# Revit family: 7. Электрические нагреватели UTR ELN
name_source: partatom
category: Оборудование
revit_build: Autodesk Revit 2016 (Build: 20151209_0715(x64)
units: mm (PartAtom-declared; Revit-internal decimal feet)

## family parameters
Всегда вертикально = Да
На основе рабочей плоскости = Нет
Общий = Нет
При загрузке вырезать с полостями = Нет
Размер круглого соединителя = Использовать диаметр
Тип детали = Нормальный
Точка расчета площади = Нет

## types (25) — shared parameters
h = 60 мм
Единица измерения = шт.
Завод изготовитель = KORF
Ключевая пометка = Вентиляция
Наименование и тех.хар-ка = Электрический нагреватель воздуха
Раздел = ОВ
Синий = Синий
высота ножек = 50 мм

## per-type parameters (varying)
| type | А | А1 | Б | Б1 | Г | Д | Д1 | Масса единицы | Материал | Мощность, кВт | Сила тока J, А | Силовой кабель | Тип, марка, обозначение | высота | размер В | ширина |
| 50-25 ELN/7,5 | 710 мм | 690 мм | 470 мм | 450 мм | 395 мм | 510 мм | 490 мм | 30 | Сталь серая | 8 Вт | 11,3 | ВВГ 4х2,5/1 | UTR 50-25 ELN/7,5 | 500 мм | 635 мм | 250 мм |
| 50-25 ELN/15 | 710 мм | 690 мм | 470 мм | 450 мм | 395 мм | 610 мм | 590 мм | 36 | Сталь серая | 15 Вт | 22,6 | ВВГ 4х2,5/2 | UTR 50-25 ELN/15 | 500 мм | 635 мм | 250 мм |
| 50-25 ELN/22,5 | 710 мм | 690 мм | 470 мм | 450 мм | 395 мм | 710 мм | 690 мм | 43 | Сталь серая | 23 Вт | 33,9 | ВВГ 4х2,5/2 | UTR 50-25 ELN/22,5 | 500 мм | 635 мм | 250 мм |
| 50-30 ELN/7,5 | 710 мм | 690 мм | 520 мм | 500 мм | 445 мм | 510 мм | 490 мм | 31 | Сталь серая | 8 Вт | 11,3 | ВВГ 4х2,5/1 | UTR 50-30 ELN/7,5 | 500 мм | 635 мм | 300 мм |
| 50-30 ELN/15 | 710 мм | 690 мм | 520 мм | 500 мм | 445 мм | 610 мм | 590 мм | 38 | Сталь серая | 15 Вт | 22,6 | ВВГ 4х2,5/2 | UTR 50-30 ELN/15 | 500 мм | 635 мм | 300 мм |
| 50-30 ELN/22,5 | 710 мм | 690 мм | 520 мм | 500 мм | 445 мм | 710 мм | 690 мм | 44 | Сталь серая | 23 Вт | 33,9 | ВВГ 4х2,5/2 | UTR 50-30 ELN/22,5 | 500 мм | 635 мм | 300 мм |
| 60-30 ELN/15 | 810 мм | 790 мм | 520 мм | 500 мм | 445 мм | 610 мм | 590 мм | 42 | Сталь серая | 15 Вт | 22,6 | ВВГ 4х2,5/2 | UTR 60-30 ELN/15 | 600 мм | 735 мм | 300 мм |
| 60-30 ELN/22,5 | 810 мм | 790 мм | 520 мм | 500 мм | 445 мм | 710 мм | 690 мм | 48 | Сталь серая | 23 Вт | 33.9 | ВВГ 4х2,5/2 | UTR 60-30 ELN/22,5 | 600 мм | 735 мм | 300 мм |
| 60-30 ELN/30 | 810 мм | 790 мм | 520 мм | 500 мм | 445 мм | 840 мм | 820 мм | 57 | Сталь серая | 30 Вт | 45.1 | ВВГ 4х6/2 | UTR 60-30 ELN/30 | 600 мм | 735 мм | 300 мм |
| 60-35 ELN/15 | 810 мм | 790 мм | 570 мм | 550 мм | 495 мм | 610 мм | 590 мм | 43 | Сталь серая | 15 Вт | 22,6 | ВВГ 4х2,5/2 | UTR 60-35 ELN/15 | 600 мм | 735 мм | 350 мм |
| 60-35 ELN/22,5 | 810 мм | 790 мм | 570 мм | 550 мм | 495 мм | 710 мм | 690 мм | 50 | Сталь серая | 23 Вт | 33.9 | ВВГ 4х2,5/2 | UTR 60-35 ELN/22,5 | 600 мм | 735 мм | 350 мм |
| 60-35 ELN/30 | 810 мм | 790 мм | 570 мм | 550 мм | 495 мм | 840 мм | 820 мм | 59 | Сталь серая | 30 Вт | 45.1 | ВВГ 4х2,5/2 | UTR 60-35 ELN/30 | 600 мм | 735 мм | 350 мм |
| 70-40 ELN/15 | 910 мм | 890 мм | 620 мм | 600 мм | 545 мм | 610 мм | 590 мм | 48 | Сталь серая | 15 Вт | 22.6 | ВВГ 4х2,5/2 | UTR 70-40 ELN/15 | 700 мм | 835 мм | 400 мм |
| 70-40 ELN/30 | 910 мм | 890 мм | 620 мм | 600 мм | 545 мм | 610 мм | 590 мм | 48 | Сталь серая | 30 Вт | 45.1 | ВВГ 4х6/2 | UTR 70-40 ELN/30 | 700 мм | 835 мм | 400 мм |
| 70-40 ELN/45 | 910 мм | 890 мм | 620 мм | 600 мм | 545 мм | 840 мм | 820 мм | 69 | Сталь серая | 45 Вт | 67.6 | ВВГ 4х10/2 | UTR 70-40 ELN/45 | 700 мм | 835 мм | 400 мм |
| 70-40 ELN/60 | 910 мм | 890 мм | 620 мм | 600 мм | 545 мм | 840 мм | 820 мм | 69 | Сталь серая | 60 Вт | 90.1 | ВВГ 4х10/2 | UTR70-40 ELN/60 | 700 мм | 835 мм | 400 мм |
| 80-50 ELN/15 | 1010 мм | 990 мм | 720 мм | 700 мм | 645 мм | 610 мм | 590 мм | 54 | Сталь серая | 15 Вт | 22.6 | ВВГ 4х2.5/2 | UTR 80-50 ELN/15 | 800 мм | 935 мм | 500 мм |
| 80-50 ELN/30 | 1010 мм | 990 мм | 720 мм | 700 мм | 645 мм | 610 мм | 590 мм | 54 | Сталь серая | 30 Вт | 45.1 | ВВГ 4х6/2 | UTR 80-50 ELN/30 | 800 мм | 935 мм | 500 мм |
| 80-50 ELN/45 | 1010 мм | 990 мм | 720 мм | 700 мм | 645 мм | 840 мм | 820 мм | 74 | Сталь серая | 45 Вт | 67.6 | ВВГ 4х10/2 | UTR 80-50 ELN/45 | 800 мм | 935 мм | 500 мм |
| 80-50 ELN/60 | 1010 мм | 990 мм | 720 мм | 700 мм | 645 мм | 840 мм | 820 мм | 74 | Сталь серая | 60 Вт | 90.1 | ВВГ 4х10/2 | UTR 80-50 ELN/60 | 800 мм | 935 мм | 500 мм |
| 90-50 ELN/30 | 1125 мм | 1105 мм | 740 мм | 720 мм | 645 мм | 610 мм | 590 мм | 61 | Сталь серая | 30 Вт | 45.1 | ВВГ 4х6/2 | UTR 90-50 ELN/30 | 900 мм | 1050 мм | 500 мм |
| 90-50 ELN/45 | 1125 мм | 1105 мм | 740 мм | 720 мм | 645 мм | 840 мм | 820 мм | 82 | Сталь серая | 45 Вт | 67.6 | ВВГ 4х10/2 | UTR 90-50 ELN/45 | 900 мм | 1050 мм | 500 мм |
| 90-50 ELN/60 | 1125 мм | 1105 мм | 740 мм | 720 мм | 645 мм | 840 мм | 820 мм | 82 | RAL 0000 Серый металл | 60 Вт | 90.1 | ВВГ 4х10/2 | UTR 90-50 ELN/60 | 900 мм | 1050 мм | 500 мм |
| 100-50 ELN/45 | 1225 мм | 1205 мм | 740 мм | 720 мм | 665 мм | 840 мм | 820 мм | 86 | Сталь серая | 45 Вт | 67.6 | ВВГ 4х10/2 | UTR 100-50 ELN/45 | 1000 мм | 1150 мм | 500 мм |
| 100-50 ELN/60 | 1225 мм | 1205 мм | 740 мм | 720 мм | 665 мм | 840 мм | 820 мм | 86 | Сталь серая | 60 Вт | 90.1 | ВВГ 4х10/2 | UTR 100-50 ELN/60 | 1000 мм | 1150 мм | 500 мм |
